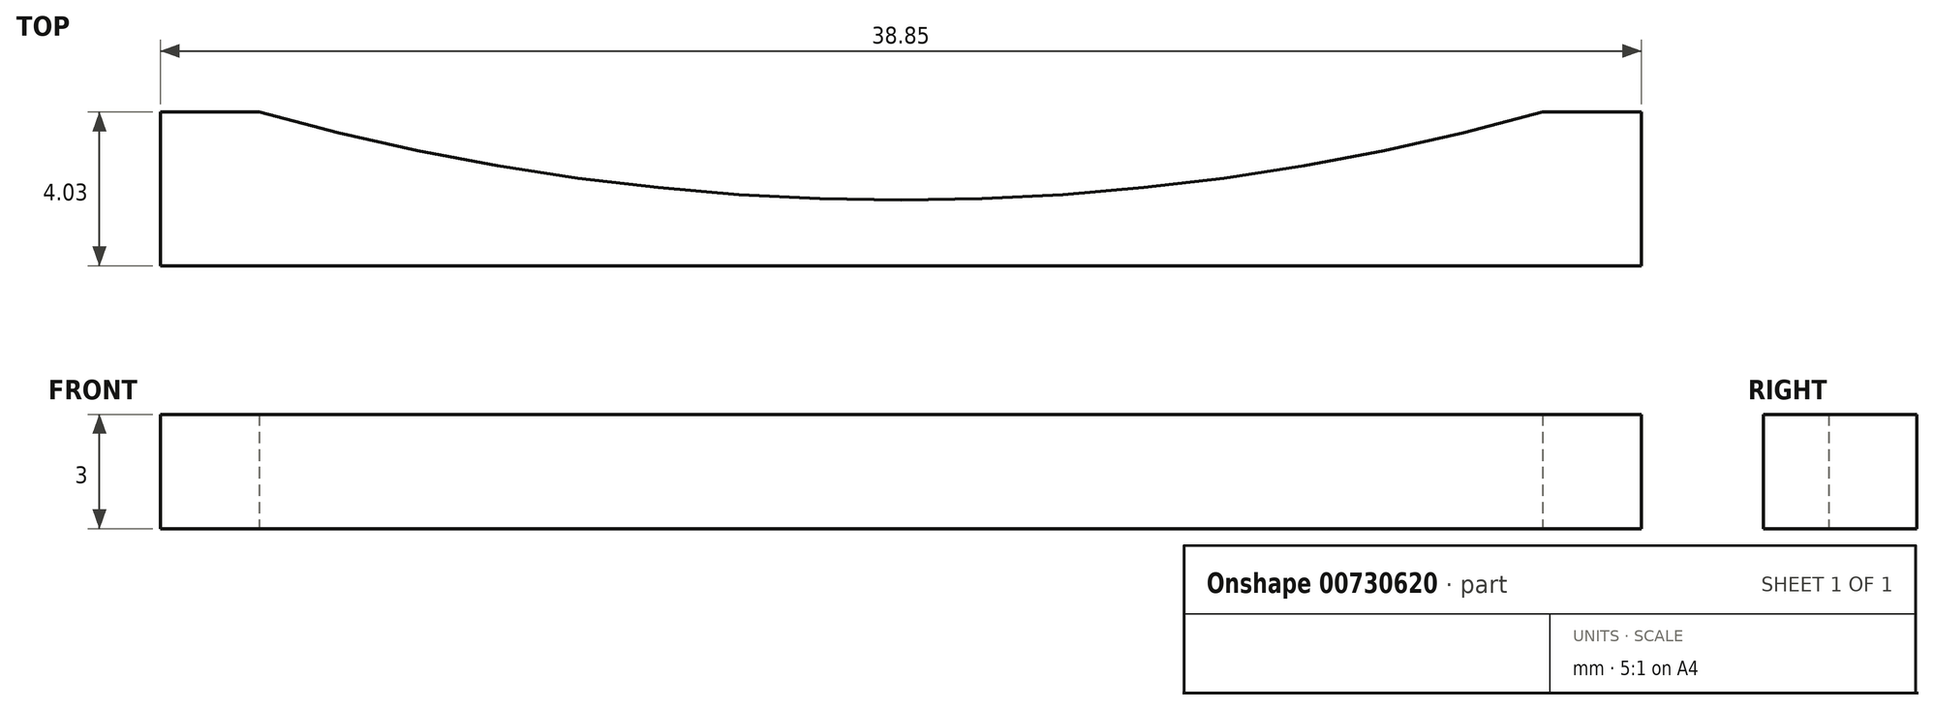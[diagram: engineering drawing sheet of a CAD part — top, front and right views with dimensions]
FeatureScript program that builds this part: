
annotation { "Feature Type Name" : "Feature", "Feature Type Description" : "" }
export const myFeature = defineFeature(function(context is Context, id is Id, definition is map)
    precondition{}
    {
        {
            var Q0;
            Q0=qCreatedBy(makeId("Top.planeOp"),FACE);
            var sketch = newSketch(context, id + "F0", { "sketchPlane" : qUnion([Q0])});
            skLineSegment(sketch, "E0.top", {"start": v(-21.73, 4.75) * mm, "end": v(17.12, 4.75) * mm});
            skLineSegment(sketch, "E0.left", {"start": v(-21.73, 8.78) * mm, "end": v(-21.73, 4.75) * mm});
            skLineSegment(sketch, "E0.right", {"start": v(17.12, 8.78) * mm, "end": v(17.12, 4.75) * mm});
            skLineSegment(sketch, "E1", {"start": v(-21.73, 8.78) * mm, "end": v(-19.14, 8.78) * mm});
            skLineSegment(sketch, "E2", {"start": v(17.12, 8.78) * mm, "end": v(14.53, 8.78) * mm});
            skArc(sketch, "E3", {"start": v(-19.14, 8.78) * mm, "mid": v(-2.3, 6.47) * mm, "end": v(14.53, 8.78) * mm});
            skSolve(sketch);
        }
        {
            var Q0;
            Q0=makeQuery(id+"F0.imprint","IMPRINT",FACE,{"disambiguationData":[TD([[makeQuery(id+"F0.imprint","IMPRINT",EDGE,{"derivedFrom":sQuery(id+"F0.wireOp",EDGE,"E0.top")}),1.0]])]});
            extrude(context, id + "F1", {"entities" : qUnion([Q0]), "depth" : 3 * mm, "offsetDistance" : 25 * mm});
        }
    });
